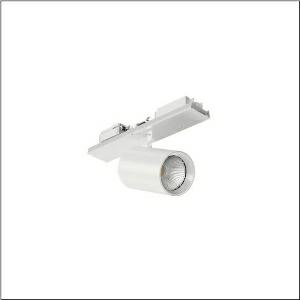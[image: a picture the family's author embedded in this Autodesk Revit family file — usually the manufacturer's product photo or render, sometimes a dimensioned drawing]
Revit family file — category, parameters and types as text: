
# Revit family: licross_spot_31_51sl13da43b
name_source: partatom
category: Lighting Fixtures
units: mm (PartAtom-declared; Revit-internal decimal feet)

## family parameters
Cut with Voids When Loaded = No
Host = Face
Light Source = No
Part Type = Normal
Room Calculation Point = No
Round Connector Dimension = Use Diameter
Shared = No

## types (1)
- --- (1 x LED, 3680 lm, 28.6 W, 4000K)
    Apparent Load = 29 VA
    CIE Flux Codes = 92 97 99 100 100
    Color Rendering = 90
    Color Temperature = 4000K
    Default Elevation = 1800 mm
    Description = Licross Spot 31, directional spotlight, light control with lens, of plastic, LED rated luminous flux: 3.680lm, light colour: 940, with plug, 5-pole, mains connection: 220..240V, AC, 50/60Hz, of aluminium, traffic white (RAL 9016), length: 300mm, diameter: 90mm, protection rating (complete): IP20, insulation class (complete): insulation class I (protective earthing), certification: CE, packaging unit: 1 piece
    Height = 175 mm
    Lamp = 1 x LED
    Lamp Light Flux = 3680 lm
    Lamp Power = 28.6 W
    Lamp count = 1
    Length = 90 mm
    Luminous efficacy = 129 lm/W
    Manufacturer = Siteco
    ModVariant = No
    Model = 51SL13DA43B
    Mounting Place = Ceiling
    Mounting Type = Pendant
    Number of Poles = 1
    OnlyDefault = Yes
    Power Factor = 1
    Product Name = Licross Spot 31
    Product group = directional spotlight
    ProductGroupID = 905
    Protection Class = Protection class I
    Protection Degree = IP 20
    RLX_Detail_Level = 1
    RLX_Emergency_Light_Flux = 0 lm
    RLX_Emergency_Type = 0
    RLX_Emergency_Type_DB = No
    RlxData = <blob elided: 14765 chars, md5=3a0590c7>
    Socket = socket
    Standby Power = 0 W
    System Light Flux = 3680 lm
    System Power = 29 W
    Type Comments = factory setting: luminous flux: 100 % | (ON | ON | ON) | 700 mA
    Type Image = l_1245720.jpg
    URL = http://relux.com
    VarID = @adj_131769
    Voltage = 0 V
    Weight = 0.00 kg
    Width = 0 mm  [stored 0 ft]

note: [stored X ft] marks values corroborated as IEEE doubles in the binary element streams (Revit-internal decimal feet)

## geometry (parser evidence)
native form markers: Sweep x11
no freeform markers — native parametric forms only
